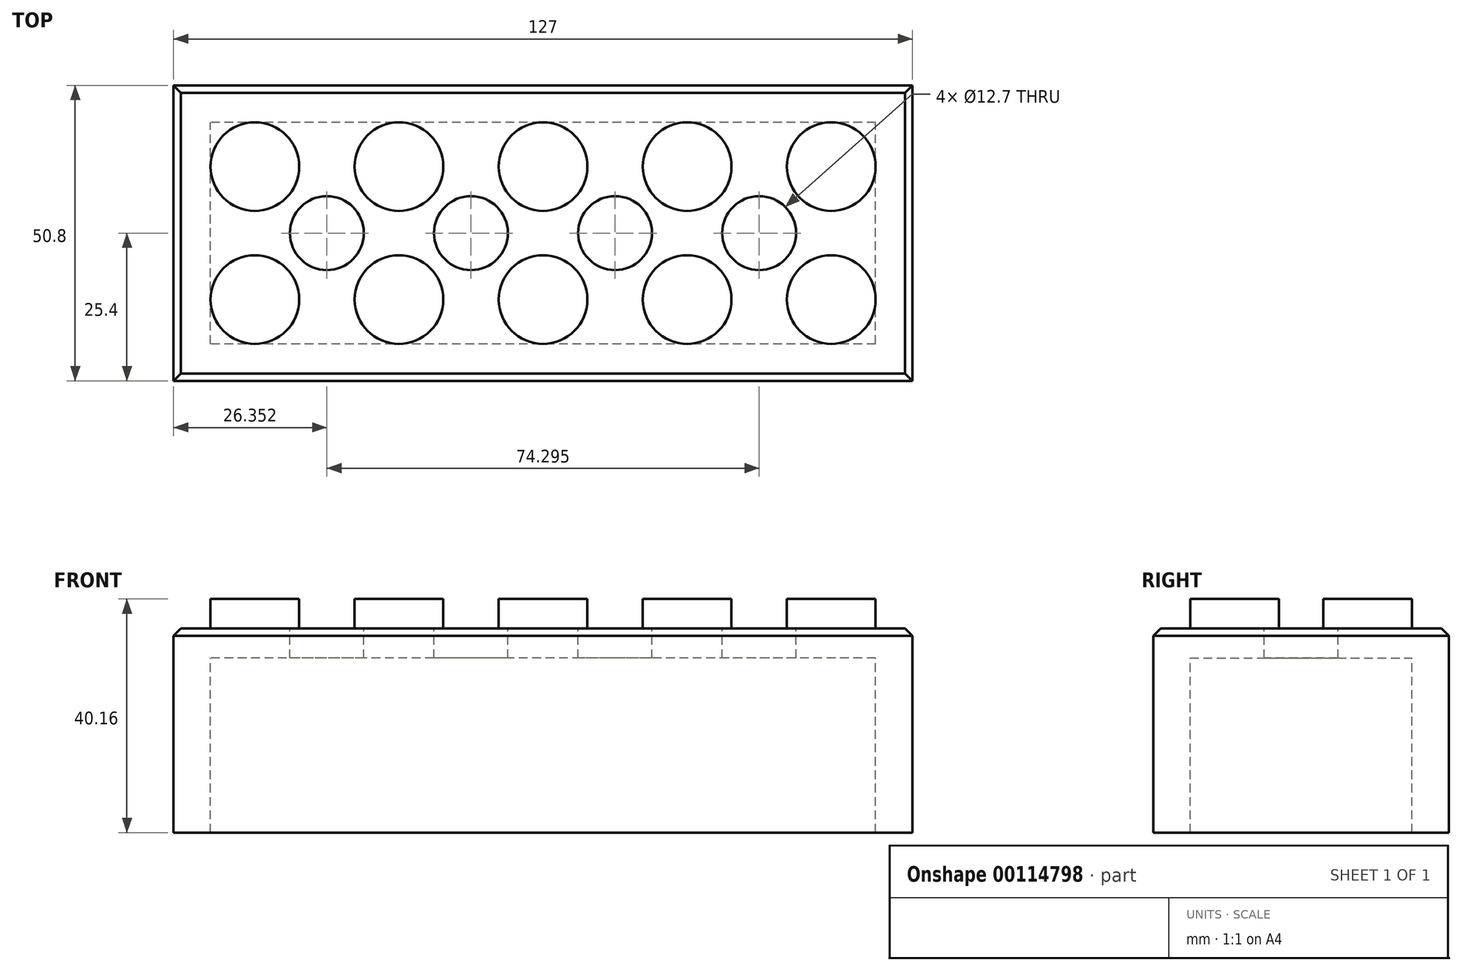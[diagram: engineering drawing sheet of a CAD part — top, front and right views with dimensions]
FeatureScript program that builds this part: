
annotation { "Feature Type Name" : "Feature", "Feature Type Description" : "" }
export const myFeature = defineFeature(function(context is Context, id is Id, definition is map)
    precondition{}
    {
        {
            var Q0;
            Q0=qCreatedBy(makeId("Top.planeOp"),FACE);
            var sketch = newSketch(context, id + "F0", { "sketchPlane" : qUnion([Q0])});
            skLineSegment(sketch, "E0.bottom", {"start": v(63.5, -25.4) * mm, "end": v(-63.5, -25.4) * mm});
            skLineSegment(sketch, "E0.top", {"start": v(63.5, 25.4) * mm, "end": v(-63.5, 25.4) * mm});
            skLineSegment(sketch, "E0.left", {"start": v(63.5, -25.4) * mm, "end": v(63.5, 25.4) * mm});
            skLineSegment(sketch, "E0.right", {"start": v(-63.5, -25.4) * mm, "end": v(-63.5, 25.4) * mm});
            skPoint(sketch, "E0.middle", {"position": v(0, 0) * mm});
            skLineSegment(sketch, "E1.bottom", {"start": v(57.15, -19.05) * mm, "end": v(-57.15, -19.05) * mm});
            skLineSegment(sketch, "E1.top", {"start": v(57.15, 19.05) * mm, "end": v(-57.15, 19.05) * mm});
            skLineSegment(sketch, "E1.left", {"start": v(57.15, -19.05) * mm, "end": v(57.15, 19.05) * mm});
            skLineSegment(sketch, "E1.right", {"start": v(-57.15, -19.05) * mm, "end": v(-57.15, 19.05) * mm});
            skSolve(sketch);
        }
        {
            var Q0;
            Q0=makeQuery(id+"F0.imprint","IMPRINT",FACE,{"disambiguationData":[TD([[makeQuery(id+"F0.imprint","IMPRINT",EDGE,{"derivedFrom":sQuery(id+"F0.wireOp",EDGE,"E0.bottom")}),-1.0]])]});
            extrude(context, id + "F1", {"entities" : qUnion([Q0]), "flatOperationType" : FlatOperationType.REMOVE, "oppositeDirection" : true, "offsetDistance" : 25 * mm, "depth" : 30 * mm, "domain" : OperationDomain.MODEL});
        }
        {
            var Q0;
            Q0=makeQuery(id+"F0.imprint","IMPRINT",FACE,{"disambiguationData":[TD([[makeQuery(id+"F0.imprint","IMPRINT",EDGE,{"derivedFrom":sQuery(id+"F0.wireOp",EDGE,"E1.bottom")}),-1.0]])]});
            var Q1;
            Q1=makeQuery(id+"F0.imprint","IMPRINT",FACE,{"disambiguationData":[TD([[makeQuery(id+"F0.imprint","IMPRINT",EDGE,{"derivedFrom":sQuery(id+"F0.wireOp",EDGE,"E0.bottom")}),-1.0]])]});
            extrude(context, id + "F2", {"entities" : qUnion([Q0, Q1]), "operationType" : NewBodyOperationType.ADD, "depth" : 5.08 * mm});
        }
        {
            var Q0;
            Q0=makeQuery(id+"F2.opExtrude","CAP_FACE",FACE,{"disambiguationData":[OSD([sQuery(id+"F0.wireOp",EDGE,"E0.bottom"),sQuery(id+"F0.wireOp",EDGE,"E0.top"),sQuery(id+"F0.wireOp",EDGE,"E0.left"),sQuery(id+"F0.wireOp",EDGE,"E0.right")])],"isStart":false});
            var sketch = newSketch(context, id + "F3", { "sketchPlane" : qUnion([Q0])});
            skCircle(sketch, "E2", {"center": v(-49.53, 11.43) * mm, "radius": 7.62 * mm});
            skLineSegment(sketch, "E3", {"start": v(-63.5, 25.4) * mm, "end": v(-63.5, 19.05) * mm, "construction": true});
            skLineSegment(sketch, "E4", {"start": v(-63.5, 19.05) * mm, "end": v(63.5, 19.05) * mm, "construction": true});
            skLineSegment(sketch, "E5", {"start": v(-57.15, 19.05) * mm, "end": v(-57.15, -25.4) * mm, "construction": true});
            skCircle(sketch, "E6.0.1.0", {"center": v(-49.53, -11.43) * mm, "radius": 7.62 * mm});
            skCircle(sketch, "E6.1.0.0", {"center": v(-24.76, 11.43) * mm, "radius": 7.62 * mm});
            skCircle(sketch, "E6.1.1.0", {"center": v(-24.76, -11.43) * mm, "radius": 7.62 * mm});
            skCircle(sketch, "E6.2.0.0", {"center": v(0, 11.43) * mm, "radius": 7.62 * mm});
            skCircle(sketch, "E6.2.1.0", {"center": v(0, -11.43) * mm, "radius": 7.62 * mm});
            skCircle(sketch, "E6.3.0.0", {"center": v(24.77, 11.43) * mm, "radius": 7.62 * mm});
            skCircle(sketch, "E6.3.1.0", {"center": v(24.77, -11.43) * mm, "radius": 7.62 * mm});
            skCircle(sketch, "E6.4.0.0", {"center": v(49.53, 11.43) * mm, "radius": 7.62 * mm});
            skCircle(sketch, "E6.4.1.0", {"center": v(49.53, -11.43) * mm, "radius": 7.62 * mm});
            skLineSegment(sketch, "E6.direction1", {"start": v(-49.53, 11.43) * mm, "end": v(-24.76, 11.43) * mm, "construction": true});
            skLineSegment(sketch, "E6.direction2", {"start": v(-49.53, 11.43) * mm, "end": v(-49.53, -11.43) * mm, "construction": true});
            skLineSegment(sketch, "E7", {"start": v(-24.76, -11.43) * mm, "end": v(-49.53, 11.43) * mm, "construction": true});
            skLineSegment(sketch, "E8", {"start": v(-24.77, 11.43) * mm, "end": v(-49.53, -11.43) * mm, "construction": true});
            skCircle(sketch, "E9", {"center": v(-37.15, 0) * mm, "radius": 6.35 * mm});
            skCircle(sketch, "E10.1.0.0", {"center": v(-12.38, 0) * mm, "radius": 6.35 * mm});
            skCircle(sketch, "E10.2.0.0", {"center": v(12.38, 0) * mm, "radius": 6.35 * mm});
            skCircle(sketch, "E10.3.0.0", {"center": v(37.15, 0) * mm, "radius": 6.35 * mm});
            skLineSegment(sketch, "E10.direction1", {"start": v(-37.15, 0) * mm, "end": v(-12.38, 0) * mm, "construction": true});
            skSolve(sketch);
        }
        {
            var Q0;
            Q0=makeQuery(id+"F2.opExtrude","CAP_EDGE",EDGE,{"disambiguationData":[OSD([sQuery(id+"F0.wireOp",EDGE,"E0.top")])],"isStart":false});
            var Q1;
            Q1=makeQuery(id+"F2.opExtrude","CAP_EDGE",EDGE,{"disambiguationData":[OSD([sQuery(id+"F0.wireOp",EDGE,"E0.left")])],"isStart":false});
            var Q2;
            Q2=makeQuery(id+"F2.opExtrude","CAP_EDGE",EDGE,{"disambiguationData":[OSD([sQuery(id+"F0.wireOp",EDGE,"E0.bottom")])],"isStart":false});
            var Q3;
            Q3=makeQuery(id+"F2.opExtrude","CAP_EDGE",EDGE,{"disambiguationData":[OSD([sQuery(id+"F0.wireOp",EDGE,"E0.right")])],"isStart":false});
            chamfer(context, id + "F4", {"entities" : qUnion([Q0, Q1, Q2, Q3]), "width" : 1.27 * mm, "tangentPropagation" : true});
        }
        {
            var Q0;
            Q0=makeQuery(id+"F3.imprint","IMPRINT",FACE,{"disambiguationData":[TD([[makeQuery(id+"F3.imprint","IMPRINT",EDGE,{"derivedFrom":sQuery(id+"F3.wireOp",EDGE,"E2")}),1.0]])]});
            var Q1;
            Q1=makeQuery(id+"F3.imprint","IMPRINT",FACE,{"disambiguationData":[TD([[makeQuery(id+"F3.imprint","IMPRINT",EDGE,{"derivedFrom":sQuery(id+"F3.wireOp",EDGE,"E6.1.0.0")}),1.0]])]});
            var Q2;
            Q2=makeQuery(id+"F3.imprint","IMPRINT",FACE,{"disambiguationData":[TD([[makeQuery(id+"F3.imprint","IMPRINT",EDGE,{"derivedFrom":sQuery(id+"F3.wireOp",EDGE,"E6.2.0.0")}),1.0]])]});
            var Q3;
            Q3=makeQuery(id+"F3.imprint","IMPRINT",FACE,{"disambiguationData":[TD([[makeQuery(id+"F3.imprint","IMPRINT",EDGE,{"derivedFrom":sQuery(id+"F3.wireOp",EDGE,"E6.4.0.0")}),1.0]])]});
            var Q4;
            Q4=makeQuery(id+"F3.imprint","IMPRINT",FACE,{"disambiguationData":[TD([[makeQuery(id+"F3.imprint","IMPRINT",EDGE,{"derivedFrom":sQuery(id+"F3.wireOp",EDGE,"E6.3.0.0")}),1.0]])]});
            var Q5;
            Q5=makeQuery(id+"F3.imprint","IMPRINT",FACE,{"disambiguationData":[TD([[makeQuery(id+"F3.imprint","IMPRINT",EDGE,{"derivedFrom":sQuery(id+"F3.wireOp",EDGE,"E6.3.1.0")}),1.0]])]});
            var Q6;
            Q6=makeQuery(id+"F3.imprint","IMPRINT",FACE,{"disambiguationData":[TD([[makeQuery(id+"F3.imprint","IMPRINT",EDGE,{"derivedFrom":sQuery(id+"F3.wireOp",EDGE,"E6.2.1.0")}),1.0]])]});
            var Q7;
            Q7=makeQuery(id+"F3.imprint","IMPRINT",FACE,{"disambiguationData":[TD([[makeQuery(id+"F3.imprint","IMPRINT",EDGE,{"derivedFrom":sQuery(id+"F3.wireOp",EDGE,"E6.1.1.0")}),1.0]])]});
            var Q8;
            Q8=makeQuery(id+"F3.imprint","IMPRINT",FACE,{"disambiguationData":[TD([[makeQuery(id+"F3.imprint","IMPRINT",EDGE,{"derivedFrom":sQuery(id+"F3.wireOp",EDGE,"E6.0.1.0")}),1.0]])]});
            var Q9;
            Q9=makeQuery(id+"F3.imprint","IMPRINT",FACE,{"disambiguationData":[TD([[makeQuery(id+"F3.imprint","IMPRINT",EDGE,{"derivedFrom":sQuery(id+"F3.wireOp",EDGE,"E6.4.1.0")}),1.0]])]});
            extrude(context, id + "F5", {"entities" : qUnion([Q0, Q1, Q2, Q3, Q4, Q5, Q6, Q7, Q8, Q9]), "operationType" : NewBodyOperationType.ADD, "depth" : 5.08 * mm});
        }
        {
            var Q0;
            Q0=makeQuery(id+"F3.imprint","IMPRINT",FACE,{"disambiguationData":[TD([[makeQuery(id+"F3.imprint","IMPRINT",EDGE,{"derivedFrom":sQuery(id+"F3.wireOp",EDGE,"E10.3.0.0")}),1.0]])]});
            var Q1;
            Q1=makeQuery(id+"F3.imprint","IMPRINT",FACE,{"disambiguationData":[TD([[makeQuery(id+"F3.imprint","IMPRINT",EDGE,{"derivedFrom":sQuery(id+"F3.wireOp",EDGE,"E10.2.0.0")}),1.0]])]});
            var Q2;
            Q2=makeQuery(id+"F3.imprint","IMPRINT",FACE,{"disambiguationData":[TD([[makeQuery(id+"F3.imprint","IMPRINT",EDGE,{"derivedFrom":sQuery(id+"F3.wireOp",EDGE,"E10.1.0.0")}),1.0]])]});
            var Q3;
            Q3=makeQuery(id+"F3.imprint","IMPRINT",FACE,{"disambiguationData":[TD([[makeQuery(id+"F3.imprint","IMPRINT",EDGE,{"derivedFrom":sQuery(id+"F3.wireOp",EDGE,"E9")}),1.0]])]});
            extrude(context, id + "F6", {"entities" : qUnion([Q0, Q1, Q2, Q3]), "operationType" : NewBodyOperationType.REMOVE, "oppositeDirection" : true, "depth" : 12.7 * mm});
        }
    });
